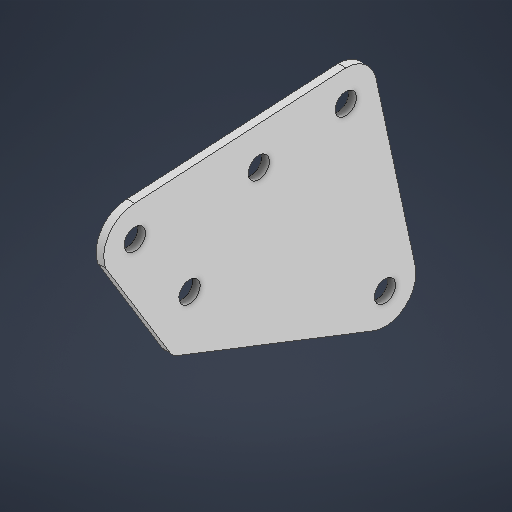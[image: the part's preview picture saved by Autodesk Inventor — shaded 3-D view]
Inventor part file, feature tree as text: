
AUTODESK INVENTOR PART (.ipt)
format: ipt  version: 2025.2 (Build 292293000, 293)  size: 190,976 bytes
history: native  units: in
note: dims shown in document units (in); Inventor stores cm internally (conversion verified against a paired STEP export)
features: extrude x1, sketch x1
ambient origin geometry x8: Origin, YZ Plane, XZ Plane, XY Plane, X Axis, Y Axis, Z Axis, Center Point
bodies: Solid1 (feature_tree)
feature tree (2):
  extrude  "Extrusion1"  Depth=0.0625in TaperAngle=0.0deg
  sketch  "Sketch1"  dims[d0=0.5in d1=0.5in d2=0.5in d3=0.125in d4=0.0625in d5=0.0in]
